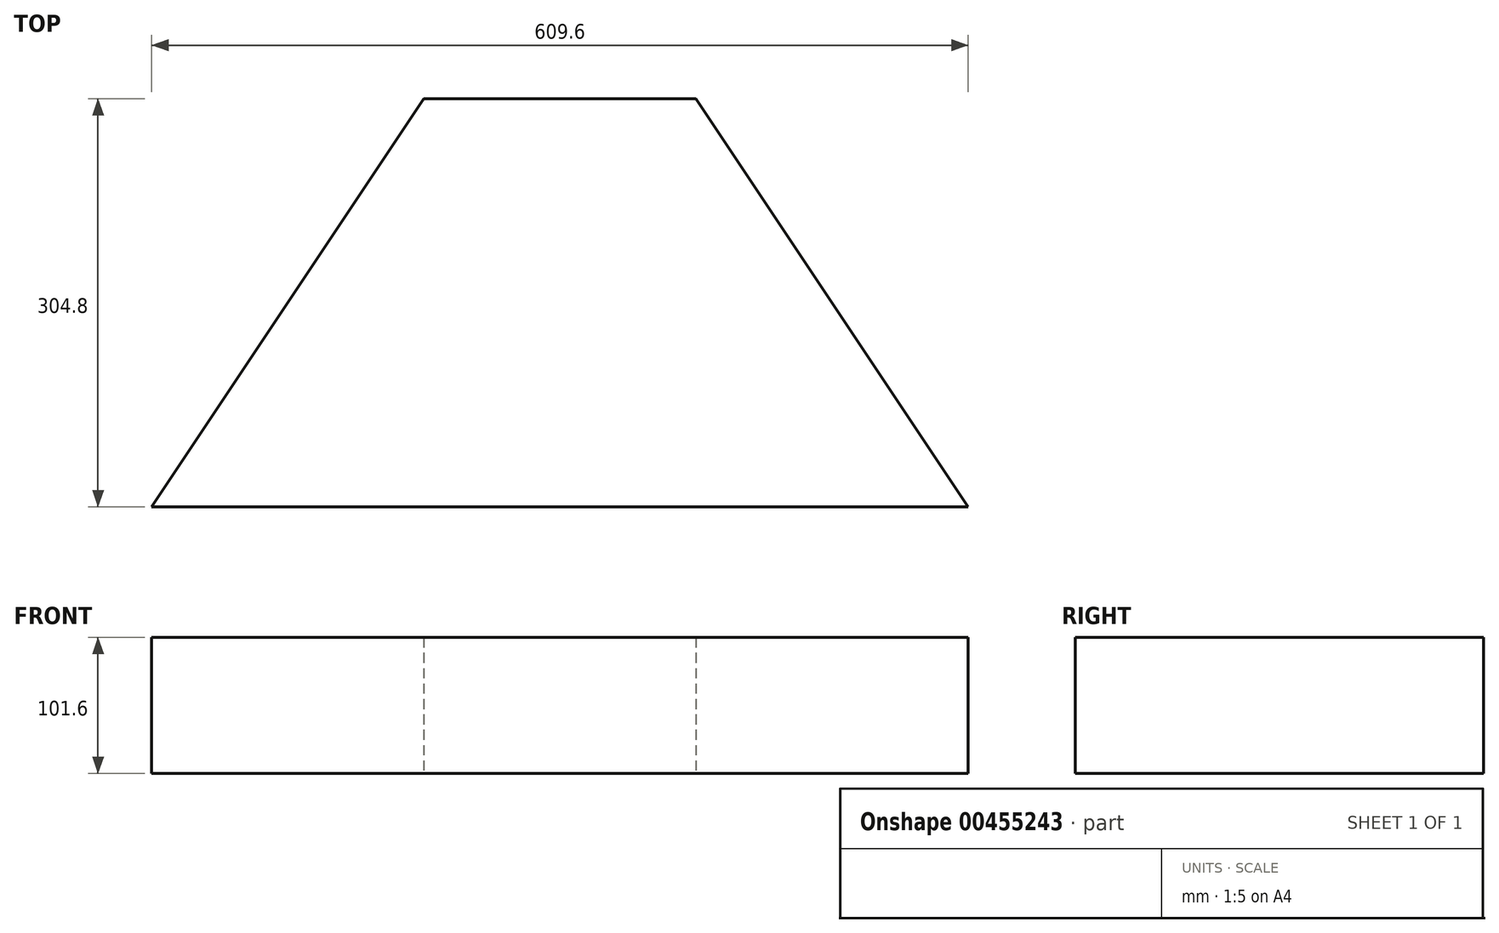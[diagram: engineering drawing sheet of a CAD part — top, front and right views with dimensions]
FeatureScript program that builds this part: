
annotation { "Feature Type Name" : "Feature", "Feature Type Description" : "" }
export const myFeature = defineFeature(function(context is Context, id is Id, definition is map)
    precondition{}
    {
        {
            var Q0;
            Q0=qCreatedBy(makeId("Top.planeOp"),FACE);
            var sketch = newSketch(context, id + "F0", { "sketchPlane" : qUnion([Q0])});
            skPoint(sketch, "E0", {"position": v(0, -156.58) * mm});
            skPoint(sketch, "E1", {"position": v(0, 148.22) * mm});
            skPoint(sketch, "E2", {"position": v(101.6, 148.22) * mm});
            skPoint(sketch, "E3", {"position": v(304.8, -156.58) * mm});
            skPoint(sketch, "E4", {"position": v(-304.8, -156.58) * mm});
            skPoint(sketch, "E5", {"position": v(-101.6, 148.22) * mm});
            skLineSegment(sketch, "E6", {"start": v(-101.6, 148.22) * mm, "end": v(-304.8, -156.58) * mm});
            skLineSegment(sketch, "E7", {"start": v(-304.8, -156.58) * mm, "end": v(304.8, -156.58) * mm});
            skLineSegment(sketch, "E8", {"start": v(101.6, 148.22) * mm, "end": v(304.8, -156.58) * mm});
            skLineSegment(sketch, "E9", {"start": v(101.6, 148.22) * mm, "end": v(-101.6, 148.22) * mm});
            skPoint(sketch, "E10", {"position": v(-203.2, -4.18) * mm});
            skPoint(sketch, "E11", {"position": v(203.2, -4.18) * mm});
            skSolve(sketch);
        }
        {
            var Q0;
            Q0 = qSketchRegion(id + "F0", true);
            extrude(context, id + "F1", {"entities" : qUnion([Q0]), "depth" : 101.6 * mm});
        }
    });
